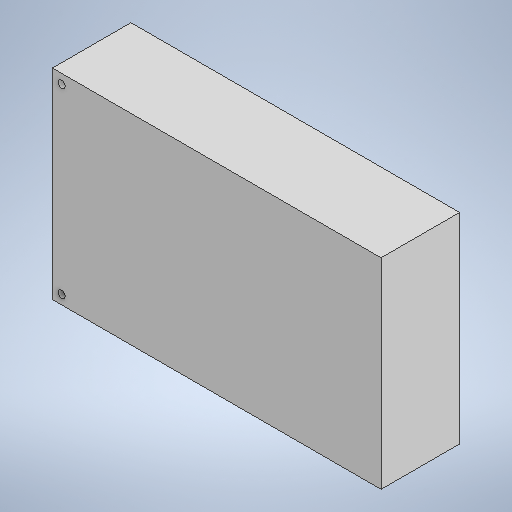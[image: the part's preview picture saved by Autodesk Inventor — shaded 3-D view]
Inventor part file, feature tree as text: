
AUTODESK INVENTOR PART (.ipt)
format: ipt  version: 2025 (Build 290162000, 162)  size: 187,904 bytes
history: native  units: in
note: dims shown in document units (in); Inventor stores cm internally (conversion verified against a paired STEP export)
features: other x1, extrude x1, sketch x1
ambient origin geometry x8: Origin, YZ Plane, XZ Plane, XY Plane, X Axis, Y Axis, Z Axis, Center Point
bodies: Body1 (feature_tree)
feature tree (3):
  other  "솔리드1"
  extrude  "돌출1"  Depth=6.2598in
  sketch  "스케치1"
